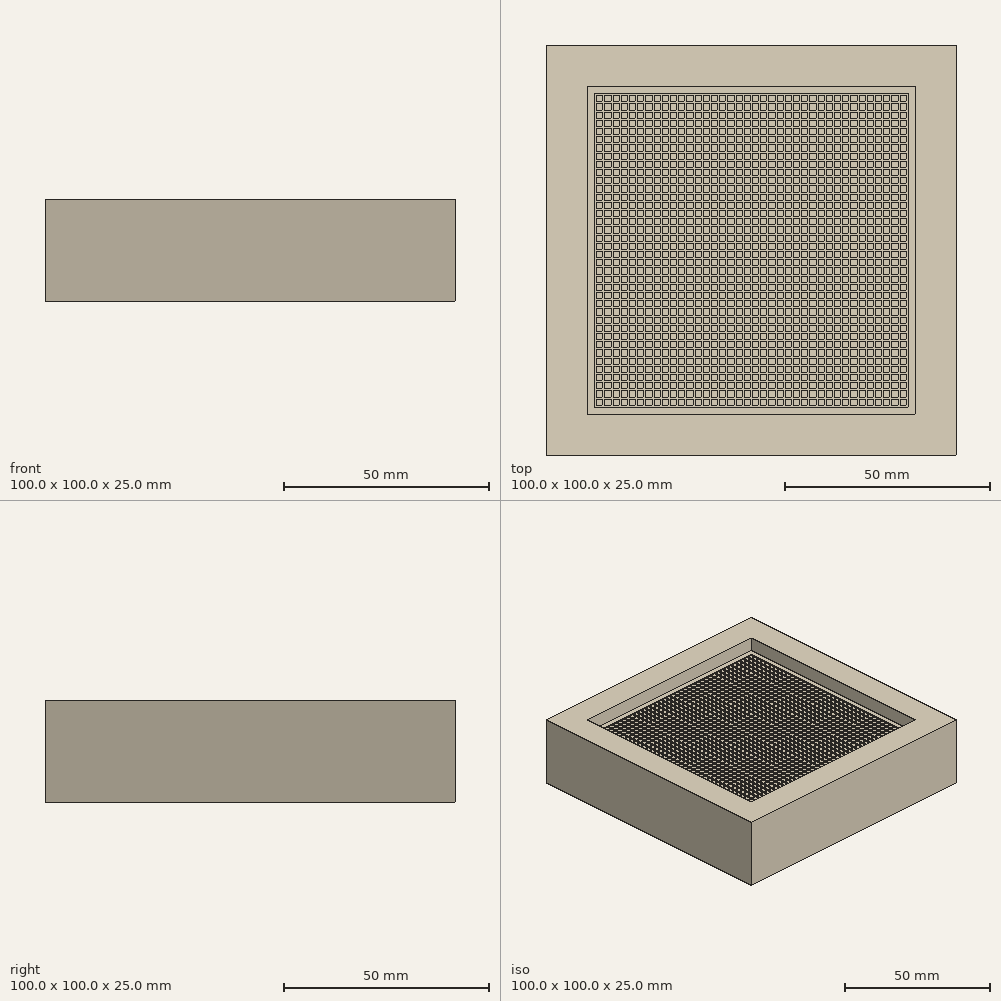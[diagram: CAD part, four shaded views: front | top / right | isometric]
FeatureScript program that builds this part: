
annotation { "Feature Type Name" : "Feature", "Feature Type Description" : "" }
export const myFeature = defineFeature(function(context is Context, id is Id, definition is map)
    precondition{}
    {
        {
            var Q0;
            Q0=qCreatedBy(makeId("Top.planeOp"),FACE);
            var sketch = newSketch(context, id + "F0", { "sketchPlane" : qUnion([Q0])});
            skLineSegment(sketch, "E0.bottom", {"start": v(0, 0) * mm, "end": v(100, 0) * mm});
            skLineSegment(sketch, "E0.top", {"start": v(0, 100) * mm, "end": v(100, 100) * mm});
            skLineSegment(sketch, "E0.left", {"start": v(0, 0) * mm, "end": v(0, 100) * mm});
            skLineSegment(sketch, "E0.right", {"start": v(100, 0) * mm, "end": v(100, 100) * mm});
            skSolve(sketch);
        }
        {
            var Q0;
            Q0 = qSketchRegion(id + "F0", true);
            extrude(context, id + "F1", {"entities" : qUnion([Q0]), "depth" : 25 * mm});
        }
        {
            var Q0;
            Q0=makeQuery(id+"F1.opExtrude","CAP_FACE",FACE,{"disambiguationData":[OSD([sQuery(id+"F0.wireOp",EDGE,"E0.bottom"),sQuery(id+"F0.wireOp",EDGE,"E0.top"),sQuery(id+"F0.wireOp",EDGE,"E0.left"),sQuery(id+"F0.wireOp",EDGE,"E0.right")])],"isStart":false});
            var sketch = newSketch(context, id + "F2", { "sketchPlane" : qUnion([Q0])});
            skLineSegment(sketch, "E1.bottom", {"start": v(10, 90) * mm, "end": v(90, 90) * mm});
            skLineSegment(sketch, "E1.top", {"start": v(10, 10) * mm, "end": v(90, 10) * mm});
            skLineSegment(sketch, "E1.left", {"start": v(10, 90) * mm, "end": v(10, 10) * mm});
            skLineSegment(sketch, "E1.right", {"start": v(90, 90) * mm, "end": v(90, 10) * mm});
            skSolve(sketch);
        }
        {
            var Q0;
            Q0 = qSketchRegion(id + "F2", true);
            extrude(context, id + "F3", {"entities" : qUnion([Q0]), "operationType" : NewBodyOperationType.REMOVE, "oppositeDirection" : true, "depth" : 5 * mm});
        }
        {
            var Q0;
            Q0=makeQuery(id+"F3.boolean.opBoolean","COPY",FACE,{"derivedFrom":makeQuery(id+"F3.opExtrude","CAP_FACE",FACE,{"disambiguationData":[OSD([sQuery(id+"F2.wireOp",EDGE,"E1.bottom"),sQuery(id+"F2.wireOp",EDGE,"E1.top"),sQuery(id+"F2.wireOp",EDGE,"E1.left"),sQuery(id+"F2.wireOp",EDGE,"E1.right")])],"isStart":false})});
            var sketch = newSketch(context, id + "F4", { "sketchPlane" : qUnion([Q0])});
            skLineSegment(sketch, "E2.bottom", {"start": v(11.75, 88.25) * mm, "end": v(12.25, 88.25) * mm});
            skLineSegment(sketch, "E2.top", {"start": v(11.75, 11.75) * mm, "end": v(12.25, 11.75) * mm});
            skLineSegment(sketch, "E2.left", {"start": v(11.75, 88.25) * mm, "end": v(11.75, 11.75) * mm});
            skLineSegment(sketch, "E2.right", {"start": v(12.25, 88.25) * mm, "end": v(12.25, 11.75) * mm});
            skLineSegment(sketch, "E3.1.0.0", {"start": v(13.75, 88.25) * mm, "end": v(14.25, 88.25) * mm});
            skLineSegment(sketch, "E3.1.0.1", {"start": v(13.75, 88.25) * mm, "end": v(13.75, 11.75) * mm});
            skLineSegment(sketch, "E3.1.0.2", {"start": v(14.25, 88.25) * mm, "end": v(14.25, 11.75) * mm});
            skLineSegment(sketch, "E3.1.0.3", {"start": v(13.75, 11.75) * mm, "end": v(14.25, 11.75) * mm});
            skLineSegment(sketch, "E3.2.0.0", {"start": v(15.75, 88.25) * mm, "end": v(16.25, 88.25) * mm});
            skLineSegment(sketch, "E3.2.0.1", {"start": v(15.75, 88.25) * mm, "end": v(15.75, 11.75) * mm});
            skLineSegment(sketch, "E3.2.0.2", {"start": v(16.25, 88.25) * mm, "end": v(16.25, 11.75) * mm});
            skLineSegment(sketch, "E3.2.0.3", {"start": v(15.75, 11.75) * mm, "end": v(16.25, 11.75) * mm});
            skLineSegment(sketch, "E3.3.0.0", {"start": v(17.75, 88.25) * mm, "end": v(18.25, 88.25) * mm});
            skLineSegment(sketch, "E3.3.0.1", {"start": v(17.75, 88.25) * mm, "end": v(17.75, 11.75) * mm});
            skLineSegment(sketch, "E3.3.0.2", {"start": v(18.25, 88.25) * mm, "end": v(18.25, 11.75) * mm});
            skLineSegment(sketch, "E3.3.0.3", {"start": v(17.75, 11.75) * mm, "end": v(18.25, 11.75) * mm});
            skLineSegment(sketch, "E3.4.0.0", {"start": v(19.75, 88.25) * mm, "end": v(20.25, 88.25) * mm});
            skLineSegment(sketch, "E3.4.0.1", {"start": v(19.75, 88.25) * mm, "end": v(19.75, 11.75) * mm});
            skLineSegment(sketch, "E3.4.0.2", {"start": v(20.25, 88.25) * mm, "end": v(20.25, 11.75) * mm});
            skLineSegment(sketch, "E3.4.0.3", {"start": v(19.75, 11.75) * mm, "end": v(20.25, 11.75) * mm});
            skLineSegment(sketch, "E3.5.0.0", {"start": v(21.75, 88.25) * mm, "end": v(22.25, 88.25) * mm});
            skLineSegment(sketch, "E3.5.0.1", {"start": v(21.75, 88.25) * mm, "end": v(21.75, 11.75) * mm});
            skLineSegment(sketch, "E3.5.0.2", {"start": v(22.25, 88.25) * mm, "end": v(22.25, 11.75) * mm});
            skLineSegment(sketch, "E3.5.0.3", {"start": v(21.75, 11.75) * mm, "end": v(22.25, 11.75) * mm});
            skLineSegment(sketch, "E3.6.0.0", {"start": v(23.75, 88.25) * mm, "end": v(24.25, 88.25) * mm});
            skLineSegment(sketch, "E3.6.0.1", {"start": v(23.75, 88.25) * mm, "end": v(23.75, 11.75) * mm});
            skLineSegment(sketch, "E3.6.0.2", {"start": v(24.25, 88.25) * mm, "end": v(24.25, 11.75) * mm});
            skLineSegment(sketch, "E3.6.0.3", {"start": v(23.75, 11.75) * mm, "end": v(24.25, 11.75) * mm});
            skLineSegment(sketch, "E3.7.0.0", {"start": v(25.75, 88.25) * mm, "end": v(26.25, 88.25) * mm});
            skLineSegment(sketch, "E3.7.0.1", {"start": v(25.75, 88.25) * mm, "end": v(25.75, 11.75) * mm});
            skLineSegment(sketch, "E3.7.0.2", {"start": v(26.25, 88.25) * mm, "end": v(26.25, 11.75) * mm});
            skLineSegment(sketch, "E3.7.0.3", {"start": v(25.75, 11.75) * mm, "end": v(26.25, 11.75) * mm});
            skLineSegment(sketch, "E3.8.0.0", {"start": v(27.75, 88.25) * mm, "end": v(28.25, 88.25) * mm});
            skLineSegment(sketch, "E3.8.0.1", {"start": v(27.75, 88.25) * mm, "end": v(27.75, 11.75) * mm});
            skLineSegment(sketch, "E3.8.0.2", {"start": v(28.25, 88.25) * mm, "end": v(28.25, 11.75) * mm});
            skLineSegment(sketch, "E3.8.0.3", {"start": v(27.75, 11.75) * mm, "end": v(28.25, 11.75) * mm});
            skLineSegment(sketch, "E3.9.0.0", {"start": v(29.75, 88.25) * mm, "end": v(30.25, 88.25) * mm});
            skLineSegment(sketch, "E3.9.0.1", {"start": v(29.75, 88.25) * mm, "end": v(29.75, 11.75) * mm});
            skLineSegment(sketch, "E3.9.0.2", {"start": v(30.25, 88.25) * mm, "end": v(30.25, 11.75) * mm});
            skLineSegment(sketch, "E3.9.0.3", {"start": v(29.75, 11.75) * mm, "end": v(30.25, 11.75) * mm});
            skLineSegment(sketch, "E3.10.0.0", {"start": v(31.75, 88.25) * mm, "end": v(32.25, 88.25) * mm});
            skLineSegment(sketch, "E3.10.0.1", {"start": v(31.75, 88.25) * mm, "end": v(31.75, 11.75) * mm});
            skLineSegment(sketch, "E3.10.0.2", {"start": v(32.25, 88.25) * mm, "end": v(32.25, 11.75) * mm});
            skLineSegment(sketch, "E3.10.0.3", {"start": v(31.75, 11.75) * mm, "end": v(32.25, 11.75) * mm});
            skLineSegment(sketch, "E3.11.0.0", {"start": v(33.75, 88.25) * mm, "end": v(34.25, 88.25) * mm});
            skLineSegment(sketch, "E3.11.0.1", {"start": v(33.75, 88.25) * mm, "end": v(33.75, 11.75) * mm});
            skLineSegment(sketch, "E3.11.0.2", {"start": v(34.25, 88.25) * mm, "end": v(34.25, 11.75) * mm});
            skLineSegment(sketch, "E3.11.0.3", {"start": v(33.75, 11.75) * mm, "end": v(34.25, 11.75) * mm});
            skLineSegment(sketch, "E3.12.0.0", {"start": v(35.75, 88.25) * mm, "end": v(36.25, 88.25) * mm});
            skLineSegment(sketch, "E3.12.0.1", {"start": v(35.75, 88.25) * mm, "end": v(35.75, 11.75) * mm});
            skLineSegment(sketch, "E3.12.0.2", {"start": v(36.25, 88.25) * mm, "end": v(36.25, 11.75) * mm});
            skLineSegment(sketch, "E3.12.0.3", {"start": v(35.75, 11.75) * mm, "end": v(36.25, 11.75) * mm});
            skLineSegment(sketch, "E3.13.0.0", {"start": v(37.75, 88.25) * mm, "end": v(38.25, 88.25) * mm});
            skLineSegment(sketch, "E3.13.0.1", {"start": v(37.75, 88.25) * mm, "end": v(37.75, 11.75) * mm});
            skLineSegment(sketch, "E3.13.0.2", {"start": v(38.25, 88.25) * mm, "end": v(38.25, 11.75) * mm});
            skLineSegment(sketch, "E3.13.0.3", {"start": v(37.75, 11.75) * mm, "end": v(38.25, 11.75) * mm});
            skLineSegment(sketch, "E3.14.0.0", {"start": v(39.75, 88.25) * mm, "end": v(40.25, 88.25) * mm});
            skLineSegment(sketch, "E3.14.0.1", {"start": v(39.75, 88.25) * mm, "end": v(39.75, 11.75) * mm});
            skLineSegment(sketch, "E3.14.0.2", {"start": v(40.25, 88.25) * mm, "end": v(40.25, 11.75) * mm});
            skLineSegment(sketch, "E3.14.0.3", {"start": v(39.75, 11.75) * mm, "end": v(40.25, 11.75) * mm});
            skLineSegment(sketch, "E3.15.0.0", {"start": v(41.75, 88.25) * mm, "end": v(42.25, 88.25) * mm});
            skLineSegment(sketch, "E3.15.0.1", {"start": v(41.75, 88.25) * mm, "end": v(41.75, 11.75) * mm});
            skLineSegment(sketch, "E3.15.0.2", {"start": v(42.25, 88.25) * mm, "end": v(42.25, 11.75) * mm});
            skLineSegment(sketch, "E3.15.0.3", {"start": v(41.75, 11.75) * mm, "end": v(42.25, 11.75) * mm});
            skLineSegment(sketch, "E3.16.0.0", {"start": v(43.75, 88.25) * mm, "end": v(44.25, 88.25) * mm});
            skLineSegment(sketch, "E3.16.0.1", {"start": v(43.75, 88.25) * mm, "end": v(43.75, 11.75) * mm});
            skLineSegment(sketch, "E3.16.0.2", {"start": v(44.25, 88.25) * mm, "end": v(44.25, 11.75) * mm});
            skLineSegment(sketch, "E3.16.0.3", {"start": v(43.75, 11.75) * mm, "end": v(44.25, 11.75) * mm});
            skLineSegment(sketch, "E3.17.0.0", {"start": v(45.75, 88.25) * mm, "end": v(46.25, 88.25) * mm});
            skLineSegment(sketch, "E3.17.0.1", {"start": v(45.75, 88.25) * mm, "end": v(45.75, 11.75) * mm});
            skLineSegment(sketch, "E3.17.0.2", {"start": v(46.25, 88.25) * mm, "end": v(46.25, 11.75) * mm});
            skLineSegment(sketch, "E3.17.0.3", {"start": v(45.75, 11.75) * mm, "end": v(46.25, 11.75) * mm});
            skLineSegment(sketch, "E3.18.0.0", {"start": v(47.75, 88.25) * mm, "end": v(48.25, 88.25) * mm});
            skLineSegment(sketch, "E3.18.0.1", {"start": v(47.75, 88.25) * mm, "end": v(47.75, 11.75) * mm});
            skLineSegment(sketch, "E3.18.0.2", {"start": v(48.25, 88.25) * mm, "end": v(48.25, 11.75) * mm});
            skLineSegment(sketch, "E3.18.0.3", {"start": v(47.75, 11.75) * mm, "end": v(48.25, 11.75) * mm});
            skLineSegment(sketch, "E3.19.0.0", {"start": v(49.75, 88.25) * mm, "end": v(50.25, 88.25) * mm});
            skLineSegment(sketch, "E3.19.0.1", {"start": v(49.75, 88.25) * mm, "end": v(49.75, 11.75) * mm});
            skLineSegment(sketch, "E3.19.0.2", {"start": v(50.25, 88.25) * mm, "end": v(50.25, 11.75) * mm});
            skLineSegment(sketch, "E3.19.0.3", {"start": v(49.75, 11.75) * mm, "end": v(50.25, 11.75) * mm});
            skLineSegment(sketch, "E3.20.0.0", {"start": v(51.75, 88.25) * mm, "end": v(52.25, 88.25) * mm});
            skLineSegment(sketch, "E3.20.0.1", {"start": v(51.75, 88.25) * mm, "end": v(51.75, 11.75) * mm});
            skLineSegment(sketch, "E3.20.0.2", {"start": v(52.25, 88.25) * mm, "end": v(52.25, 11.75) * mm});
            skLineSegment(sketch, "E3.20.0.3", {"start": v(51.75, 11.75) * mm, "end": v(52.25, 11.75) * mm});
            skLineSegment(sketch, "E3.21.0.0", {"start": v(53.75, 88.25) * mm, "end": v(54.25, 88.25) * mm});
            skLineSegment(sketch, "E3.21.0.1", {"start": v(53.75, 88.25) * mm, "end": v(53.75, 11.75) * mm});
            skLineSegment(sketch, "E3.21.0.2", {"start": v(54.25, 88.25) * mm, "end": v(54.25, 11.75) * mm});
            skLineSegment(sketch, "E3.21.0.3", {"start": v(53.75, 11.75) * mm, "end": v(54.25, 11.75) * mm});
            skLineSegment(sketch, "E3.22.0.0", {"start": v(55.75, 88.25) * mm, "end": v(56.25, 88.25) * mm});
            skLineSegment(sketch, "E3.22.0.1", {"start": v(55.75, 88.25) * mm, "end": v(55.75, 11.75) * mm});
            skLineSegment(sketch, "E3.22.0.2", {"start": v(56.25, 88.25) * mm, "end": v(56.25, 11.75) * mm});
            skLineSegment(sketch, "E3.22.0.3", {"start": v(55.75, 11.75) * mm, "end": v(56.25, 11.75) * mm});
            skLineSegment(sketch, "E3.23.0.0", {"start": v(57.75, 88.25) * mm, "end": v(58.25, 88.25) * mm});
            skLineSegment(sketch, "E3.23.0.1", {"start": v(57.75, 88.25) * mm, "end": v(57.75, 11.75) * mm});
            skLineSegment(sketch, "E3.23.0.2", {"start": v(58.25, 88.25) * mm, "end": v(58.25, 11.75) * mm});
            skLineSegment(sketch, "E3.23.0.3", {"start": v(57.75, 11.75) * mm, "end": v(58.25, 11.75) * mm});
            skLineSegment(sketch, "E3.24.0.0", {"start": v(59.75, 88.25) * mm, "end": v(60.25, 88.25) * mm});
            skLineSegment(sketch, "E3.24.0.1", {"start": v(59.75, 88.25) * mm, "end": v(59.75, 11.75) * mm});
            skLineSegment(sketch, "E3.24.0.2", {"start": v(60.25, 88.25) * mm, "end": v(60.25, 11.75) * mm});
            skLineSegment(sketch, "E3.24.0.3", {"start": v(59.75, 11.75) * mm, "end": v(60.25, 11.75) * mm});
            skLineSegment(sketch, "E3.25.0.0", {"start": v(61.75, 88.25) * mm, "end": v(62.25, 88.25) * mm});
            skLineSegment(sketch, "E3.25.0.1", {"start": v(61.75, 88.25) * mm, "end": v(61.75, 11.75) * mm});
            skLineSegment(sketch, "E3.25.0.2", {"start": v(62.25, 88.25) * mm, "end": v(62.25, 11.75) * mm});
            skLineSegment(sketch, "E3.25.0.3", {"start": v(61.75, 11.75) * mm, "end": v(62.25, 11.75) * mm});
            skLineSegment(sketch, "E3.26.0.0", {"start": v(63.75, 88.25) * mm, "end": v(64.25, 88.25) * mm});
            skLineSegment(sketch, "E3.26.0.1", {"start": v(63.75, 88.25) * mm, "end": v(63.75, 11.75) * mm});
            skLineSegment(sketch, "E3.26.0.2", {"start": v(64.25, 88.25) * mm, "end": v(64.25, 11.75) * mm});
            skLineSegment(sketch, "E3.26.0.3", {"start": v(63.75, 11.75) * mm, "end": v(64.25, 11.75) * mm});
            skLineSegment(sketch, "E3.27.0.0", {"start": v(65.75, 88.25) * mm, "end": v(66.25, 88.25) * mm});
            skLineSegment(sketch, "E3.27.0.1", {"start": v(65.75, 88.25) * mm, "end": v(65.75, 11.75) * mm});
            skLineSegment(sketch, "E3.27.0.2", {"start": v(66.25, 88.25) * mm, "end": v(66.25, 11.75) * mm});
            skLineSegment(sketch, "E3.27.0.3", {"start": v(65.75, 11.75) * mm, "end": v(66.25, 11.75) * mm});
            skLineSegment(sketch, "E3.28.0.0", {"start": v(67.75, 88.25) * mm, "end": v(68.25, 88.25) * mm});
            skLineSegment(sketch, "E3.28.0.1", {"start": v(67.75, 88.25) * mm, "end": v(67.75, 11.75) * mm});
            skLineSegment(sketch, "E3.28.0.2", {"start": v(68.25, 88.25) * mm, "end": v(68.25, 11.75) * mm});
            skLineSegment(sketch, "E3.28.0.3", {"start": v(67.75, 11.75) * mm, "end": v(68.25, 11.75) * mm});
            skLineSegment(sketch, "E3.29.0.0", {"start": v(69.75, 88.25) * mm, "end": v(70.25, 88.25) * mm});
            skLineSegment(sketch, "E3.29.0.1", {"start": v(69.75, 88.25) * mm, "end": v(69.75, 11.75) * mm});
            skLineSegment(sketch, "E3.29.0.2", {"start": v(70.25, 88.25) * mm, "end": v(70.25, 11.75) * mm});
            skLineSegment(sketch, "E3.29.0.3", {"start": v(69.75, 11.75) * mm, "end": v(70.25, 11.75) * mm});
            skLineSegment(sketch, "E3.30.0.0", {"start": v(71.75, 88.25) * mm, "end": v(72.25, 88.25) * mm});
            skLineSegment(sketch, "E3.30.0.1", {"start": v(71.75, 88.25) * mm, "end": v(71.75, 11.75) * mm});
            skLineSegment(sketch, "E3.30.0.2", {"start": v(72.25, 88.25) * mm, "end": v(72.25, 11.75) * mm});
            skLineSegment(sketch, "E3.30.0.3", {"start": v(71.75, 11.75) * mm, "end": v(72.25, 11.75) * mm});
            skLineSegment(sketch, "E3.31.0.0", {"start": v(73.75, 88.25) * mm, "end": v(74.25, 88.25) * mm});
            skLineSegment(sketch, "E3.31.0.1", {"start": v(73.75, 88.25) * mm, "end": v(73.75, 11.75) * mm});
            skLineSegment(sketch, "E3.31.0.2", {"start": v(74.25, 88.25) * mm, "end": v(74.25, 11.75) * mm});
            skLineSegment(sketch, "E3.31.0.3", {"start": v(73.75, 11.75) * mm, "end": v(74.25, 11.75) * mm});
            skLineSegment(sketch, "E3.32.0.0", {"start": v(75.75, 88.25) * mm, "end": v(76.25, 88.25) * mm});
            skLineSegment(sketch, "E3.32.0.1", {"start": v(75.75, 88.25) * mm, "end": v(75.75, 11.75) * mm});
            skLineSegment(sketch, "E3.32.0.2", {"start": v(76.25, 88.25) * mm, "end": v(76.25, 11.75) * mm});
            skLineSegment(sketch, "E3.32.0.3", {"start": v(75.75, 11.75) * mm, "end": v(76.25, 11.75) * mm});
            skLineSegment(sketch, "E3.33.0.0", {"start": v(77.75, 88.25) * mm, "end": v(78.25, 88.25) * mm});
            skLineSegment(sketch, "E3.33.0.1", {"start": v(77.75, 88.25) * mm, "end": v(77.75, 11.75) * mm});
            skLineSegment(sketch, "E3.33.0.2", {"start": v(78.25, 88.25) * mm, "end": v(78.25, 11.75) * mm});
            skLineSegment(sketch, "E3.33.0.3", {"start": v(77.75, 11.75) * mm, "end": v(78.25, 11.75) * mm});
            skLineSegment(sketch, "E3.34.0.0", {"start": v(79.75, 88.25) * mm, "end": v(80.25, 88.25) * mm});
            skLineSegment(sketch, "E3.34.0.1", {"start": v(79.75, 88.25) * mm, "end": v(79.75, 11.75) * mm});
            skLineSegment(sketch, "E3.34.0.2", {"start": v(80.25, 88.25) * mm, "end": v(80.25, 11.75) * mm});
            skLineSegment(sketch, "E3.34.0.3", {"start": v(79.75, 11.75) * mm, "end": v(80.25, 11.75) * mm});
            skLineSegment(sketch, "E3.35.0.0", {"start": v(81.75, 88.25) * mm, "end": v(82.25, 88.25) * mm});
            skLineSegment(sketch, "E3.35.0.1", {"start": v(81.75, 88.25) * mm, "end": v(81.75, 11.75) * mm});
            skLineSegment(sketch, "E3.35.0.2", {"start": v(82.25, 88.25) * mm, "end": v(82.25, 11.75) * mm});
            skLineSegment(sketch, "E3.35.0.3", {"start": v(81.75, 11.75) * mm, "end": v(82.25, 11.75) * mm});
            skLineSegment(sketch, "E3.36.0.0", {"start": v(83.75, 88.25) * mm, "end": v(84.25, 88.25) * mm});
            skLineSegment(sketch, "E3.36.0.1", {"start": v(83.75, 88.25) * mm, "end": v(83.75, 11.75) * mm});
            skLineSegment(sketch, "E3.36.0.2", {"start": v(84.25, 88.25) * mm, "end": v(84.25, 11.75) * mm});
            skLineSegment(sketch, "E3.36.0.3", {"start": v(83.75, 11.75) * mm, "end": v(84.25, 11.75) * mm});
            skLineSegment(sketch, "E3.37.0.0", {"start": v(85.75, 88.25) * mm, "end": v(86.25, 88.25) * mm});
            skLineSegment(sketch, "E3.37.0.1", {"start": v(85.75, 88.25) * mm, "end": v(85.75, 11.75) * mm});
            skLineSegment(sketch, "E3.37.0.2", {"start": v(86.25, 88.25) * mm, "end": v(86.25, 11.75) * mm});
            skLineSegment(sketch, "E3.37.0.3", {"start": v(85.75, 11.75) * mm, "end": v(86.25, 11.75) * mm});
            skLineSegment(sketch, "E3.38.0.0", {"start": v(87.75, 88.25) * mm, "end": v(88.25, 88.25) * mm});
            skLineSegment(sketch, "E3.38.0.1", {"start": v(87.75, 88.25) * mm, "end": v(87.75, 11.75) * mm});
            skLineSegment(sketch, "E3.38.0.2", {"start": v(88.25, 88.25) * mm, "end": v(88.25, 11.75) * mm});
            skLineSegment(sketch, "E3.38.0.3", {"start": v(87.75, 11.75) * mm, "end": v(88.25, 11.75) * mm});
            skLineSegment(sketch, "E3.direction1", {"start": v(11.75, 88.25) * mm, "end": v(13.75, 88.25) * mm, "construction": true});
            skSolve(sketch);
        }
        {
            var Q0;
            Q0 = qSketchRegion(id + "F4", true);
            extrude(context, id + "F5", {"entities" : qUnion([Q0]), "operationType" : NewBodyOperationType.REMOVE, "oppositeDirection" : true, "depth" : 0.2 * mm});
        }
        {
            var Q0;
            Q0=makeQuery(id+"F3.boolean.opBoolean","COPY",FACE,{"derivedFrom":makeQuery(id+"F3.opExtrude","CAP_FACE",FACE,{"disambiguationData":[OSD([sQuery(id+"F2.wireOp",EDGE,"E1.bottom"),sQuery(id+"F2.wireOp",EDGE,"E1.top"),sQuery(id+"F2.wireOp",EDGE,"E1.left"),sQuery(id+"F2.wireOp",EDGE,"E1.right")])],"isStart":false})});
            var sketch = newSketch(context, id + "F6", { "sketchPlane" : qUnion([Q0])});
            skLineSegment(sketch, "E4.bottom", {"start": v(12, 88.25) * mm, "end": v(88, 88.25) * mm});
            skLineSegment(sketch, "E4.top", {"start": v(12, 87.75) * mm, "end": v(88, 87.75) * mm});
            skLineSegment(sketch, "E4.left", {"start": v(12, 88.25) * mm, "end": v(12, 87.75) * mm});
            skLineSegment(sketch, "E4.right", {"start": v(88, 88.25) * mm, "end": v(88, 87.75) * mm});
            skLineSegment(sketch, "E5.0.1.0", {"start": v(12, 85.75) * mm, "end": v(88, 85.75) * mm});
            skLineSegment(sketch, "E5.0.1.1", {"start": v(12, 86.25) * mm, "end": v(88, 86.25) * mm});
            skLineSegment(sketch, "E5.0.1.2", {"start": v(12, 86.25) * mm, "end": v(12, 85.75) * mm});
            skLineSegment(sketch, "E5.0.1.3", {"start": v(88, 86.25) * mm, "end": v(88, 85.75) * mm});
            skLineSegment(sketch, "E5.0.2.0", {"start": v(12, 83.75) * mm, "end": v(88, 83.75) * mm});
            skLineSegment(sketch, "E5.0.2.1", {"start": v(12, 84.25) * mm, "end": v(88, 84.25) * mm});
            skLineSegment(sketch, "E5.0.2.2", {"start": v(12, 84.25) * mm, "end": v(12, 83.75) * mm});
            skLineSegment(sketch, "E5.0.2.3", {"start": v(88, 84.25) * mm, "end": v(88, 83.75) * mm});
            skLineSegment(sketch, "E5.0.3.0", {"start": v(12, 81.75) * mm, "end": v(88, 81.75) * mm});
            skLineSegment(sketch, "E5.0.3.1", {"start": v(12, 82.25) * mm, "end": v(88, 82.25) * mm});
            skLineSegment(sketch, "E5.0.3.2", {"start": v(12, 82.25) * mm, "end": v(12, 81.75) * mm});
            skLineSegment(sketch, "E5.0.3.3", {"start": v(88, 82.25) * mm, "end": v(88, 81.75) * mm});
            skLineSegment(sketch, "E5.0.4.0", {"start": v(12, 79.75) * mm, "end": v(88, 79.75) * mm});
            skLineSegment(sketch, "E5.0.4.1", {"start": v(12, 80.25) * mm, "end": v(88, 80.25) * mm});
            skLineSegment(sketch, "E5.0.4.2", {"start": v(12, 80.25) * mm, "end": v(12, 79.75) * mm});
            skLineSegment(sketch, "E5.0.4.3", {"start": v(88, 80.25) * mm, "end": v(88, 79.75) * mm});
            skLineSegment(sketch, "E5.0.5.0", {"start": v(12, 77.75) * mm, "end": v(88, 77.75) * mm});
            skLineSegment(sketch, "E5.0.5.1", {"start": v(12, 78.25) * mm, "end": v(88, 78.25) * mm});
            skLineSegment(sketch, "E5.0.5.2", {"start": v(12, 78.25) * mm, "end": v(12, 77.75) * mm});
            skLineSegment(sketch, "E5.0.5.3", {"start": v(88, 78.25) * mm, "end": v(88, 77.75) * mm});
            skLineSegment(sketch, "E5.0.6.0", {"start": v(12, 75.75) * mm, "end": v(88, 75.75) * mm});
            skLineSegment(sketch, "E5.0.6.1", {"start": v(12, 76.25) * mm, "end": v(88, 76.25) * mm});
            skLineSegment(sketch, "E5.0.6.2", {"start": v(12, 76.25) * mm, "end": v(12, 75.75) * mm});
            skLineSegment(sketch, "E5.0.6.3", {"start": v(88, 76.25) * mm, "end": v(88, 75.75) * mm});
            skLineSegment(sketch, "E5.0.7.0", {"start": v(12, 73.75) * mm, "end": v(88, 73.75) * mm});
            skLineSegment(sketch, "E5.0.7.1", {"start": v(12, 74.25) * mm, "end": v(88, 74.25) * mm});
            skLineSegment(sketch, "E5.0.7.2", {"start": v(12, 74.25) * mm, "end": v(12, 73.75) * mm});
            skLineSegment(sketch, "E5.0.7.3", {"start": v(88, 74.25) * mm, "end": v(88, 73.75) * mm});
            skLineSegment(sketch, "E5.0.8.0", {"start": v(12, 71.75) * mm, "end": v(88, 71.75) * mm});
            skLineSegment(sketch, "E5.0.8.1", {"start": v(12, 72.25) * mm, "end": v(88, 72.25) * mm});
            skLineSegment(sketch, "E5.0.8.2", {"start": v(12, 72.25) * mm, "end": v(12, 71.75) * mm});
            skLineSegment(sketch, "E5.0.8.3", {"start": v(88, 72.25) * mm, "end": v(88, 71.75) * mm});
            skLineSegment(sketch, "E5.0.9.0", {"start": v(12, 69.75) * mm, "end": v(88, 69.75) * mm});
            skLineSegment(sketch, "E5.0.9.1", {"start": v(12, 70.25) * mm, "end": v(88, 70.25) * mm});
            skLineSegment(sketch, "E5.0.9.2", {"start": v(12, 70.25) * mm, "end": v(12, 69.75) * mm});
            skLineSegment(sketch, "E5.0.9.3", {"start": v(88, 70.25) * mm, "end": v(88, 69.75) * mm});
            skLineSegment(sketch, "E5.0.10.0", {"start": v(12, 67.75) * mm, "end": v(88, 67.75) * mm});
            skLineSegment(sketch, "E5.0.10.1", {"start": v(12, 68.25) * mm, "end": v(88, 68.25) * mm});
            skLineSegment(sketch, "E5.0.10.2", {"start": v(12, 68.25) * mm, "end": v(12, 67.75) * mm});
            skLineSegment(sketch, "E5.0.10.3", {"start": v(88, 68.25) * mm, "end": v(88, 67.75) * mm});
            skLineSegment(sketch, "E5.0.11.0", {"start": v(12, 65.75) * mm, "end": v(88, 65.75) * mm});
            skLineSegment(sketch, "E5.0.11.1", {"start": v(12, 66.25) * mm, "end": v(88, 66.25) * mm});
            skLineSegment(sketch, "E5.0.11.2", {"start": v(12, 66.25) * mm, "end": v(12, 65.75) * mm});
            skLineSegment(sketch, "E5.0.11.3", {"start": v(88, 66.25) * mm, "end": v(88, 65.75) * mm});
            skLineSegment(sketch, "E5.0.12.0", {"start": v(12, 63.75) * mm, "end": v(88, 63.75) * mm});
            skLineSegment(sketch, "E5.0.12.1", {"start": v(12, 64.25) * mm, "end": v(88, 64.25) * mm});
            skLineSegment(sketch, "E5.0.12.2", {"start": v(12, 64.25) * mm, "end": v(12, 63.75) * mm});
            skLineSegment(sketch, "E5.0.12.3", {"start": v(88, 64.25) * mm, "end": v(88, 63.75) * mm});
            skLineSegment(sketch, "E5.0.13.0", {"start": v(12, 61.75) * mm, "end": v(88, 61.75) * mm});
            skLineSegment(sketch, "E5.0.13.1", {"start": v(12, 62.25) * mm, "end": v(88, 62.25) * mm});
            skLineSegment(sketch, "E5.0.13.2", {"start": v(12, 62.25) * mm, "end": v(12, 61.75) * mm});
            skLineSegment(sketch, "E5.0.13.3", {"start": v(88, 62.25) * mm, "end": v(88, 61.75) * mm});
            skLineSegment(sketch, "E5.0.14.0", {"start": v(12, 59.75) * mm, "end": v(88, 59.75) * mm});
            skLineSegment(sketch, "E5.0.14.1", {"start": v(12, 60.25) * mm, "end": v(88, 60.25) * mm});
            skLineSegment(sketch, "E5.0.14.2", {"start": v(12, 60.25) * mm, "end": v(12, 59.75) * mm});
            skLineSegment(sketch, "E5.0.14.3", {"start": v(88, 60.25) * mm, "end": v(88, 59.75) * mm});
            skLineSegment(sketch, "E5.0.15.0", {"start": v(12, 57.75) * mm, "end": v(88, 57.75) * mm});
            skLineSegment(sketch, "E5.0.15.1", {"start": v(12, 58.25) * mm, "end": v(88, 58.25) * mm});
            skLineSegment(sketch, "E5.0.15.2", {"start": v(12, 58.25) * mm, "end": v(12, 57.75) * mm});
            skLineSegment(sketch, "E5.0.15.3", {"start": v(88, 58.25) * mm, "end": v(88, 57.75) * mm});
            skLineSegment(sketch, "E5.0.16.0", {"start": v(12, 55.75) * mm, "end": v(88, 55.75) * mm});
            skLineSegment(sketch, "E5.0.16.1", {"start": v(12, 56.25) * mm, "end": v(88, 56.25) * mm});
            skLineSegment(sketch, "E5.0.16.2", {"start": v(12, 56.25) * mm, "end": v(12, 55.75) * mm});
            skLineSegment(sketch, "E5.0.16.3", {"start": v(88, 56.25) * mm, "end": v(88, 55.75) * mm});
            skLineSegment(sketch, "E5.0.17.0", {"start": v(12, 53.75) * mm, "end": v(88, 53.75) * mm});
            skLineSegment(sketch, "E5.0.17.1", {"start": v(12, 54.25) * mm, "end": v(88, 54.25) * mm});
            skLineSegment(sketch, "E5.0.17.2", {"start": v(12, 54.25) * mm, "end": v(12, 53.75) * mm});
            skLineSegment(sketch, "E5.0.17.3", {"start": v(88, 54.25) * mm, "end": v(88, 53.75) * mm});
            skLineSegment(sketch, "E5.0.18.0", {"start": v(12, 51.75) * mm, "end": v(88, 51.75) * mm});
            skLineSegment(sketch, "E5.0.18.1", {"start": v(12, 52.25) * mm, "end": v(88, 52.25) * mm});
            skLineSegment(sketch, "E5.0.18.2", {"start": v(12, 52.25) * mm, "end": v(12, 51.75) * mm});
            skLineSegment(sketch, "E5.0.18.3", {"start": v(88, 52.25) * mm, "end": v(88, 51.75) * mm});
            skLineSegment(sketch, "E5.0.19.0", {"start": v(12, 49.75) * mm, "end": v(88, 49.75) * mm});
            skLineSegment(sketch, "E5.0.19.1", {"start": v(12, 50.25) * mm, "end": v(88, 50.25) * mm});
            skLineSegment(sketch, "E5.0.19.2", {"start": v(12, 50.25) * mm, "end": v(12, 49.75) * mm});
            skLineSegment(sketch, "E5.0.19.3", {"start": v(88, 50.25) * mm, "end": v(88, 49.75) * mm});
            skLineSegment(sketch, "E5.0.20.0", {"start": v(12, 47.75) * mm, "end": v(88, 47.75) * mm});
            skLineSegment(sketch, "E5.0.20.1", {"start": v(12, 48.25) * mm, "end": v(88, 48.25) * mm});
            skLineSegment(sketch, "E5.0.20.2", {"start": v(12, 48.25) * mm, "end": v(12, 47.75) * mm});
            skLineSegment(sketch, "E5.0.20.3", {"start": v(88, 48.25) * mm, "end": v(88, 47.75) * mm});
            skLineSegment(sketch, "E5.0.21.0", {"start": v(12, 45.75) * mm, "end": v(88, 45.75) * mm});
            skLineSegment(sketch, "E5.0.21.1", {"start": v(12, 46.25) * mm, "end": v(88, 46.25) * mm});
            skLineSegment(sketch, "E5.0.21.2", {"start": v(12, 46.25) * mm, "end": v(12, 45.75) * mm});
            skLineSegment(sketch, "E5.0.21.3", {"start": v(88, 46.25) * mm, "end": v(88, 45.75) * mm});
            skLineSegment(sketch, "E5.0.22.0", {"start": v(12, 43.75) * mm, "end": v(88, 43.75) * mm});
            skLineSegment(sketch, "E5.0.22.1", {"start": v(12, 44.25) * mm, "end": v(88, 44.25) * mm});
            skLineSegment(sketch, "E5.0.22.2", {"start": v(12, 44.25) * mm, "end": v(12, 43.75) * mm});
            skLineSegment(sketch, "E5.0.22.3", {"start": v(88, 44.25) * mm, "end": v(88, 43.75) * mm});
            skLineSegment(sketch, "E5.0.23.0", {"start": v(12, 41.75) * mm, "end": v(88, 41.75) * mm});
            skLineSegment(sketch, "E5.0.23.1", {"start": v(12, 42.25) * mm, "end": v(88, 42.25) * mm});
            skLineSegment(sketch, "E5.0.23.2", {"start": v(12, 42.25) * mm, "end": v(12, 41.75) * mm});
            skLineSegment(sketch, "E5.0.23.3", {"start": v(88, 42.25) * mm, "end": v(88, 41.75) * mm});
            skLineSegment(sketch, "E5.0.24.0", {"start": v(12, 39.75) * mm, "end": v(88, 39.75) * mm});
            skLineSegment(sketch, "E5.0.24.1", {"start": v(12, 40.25) * mm, "end": v(88, 40.25) * mm});
            skLineSegment(sketch, "E5.0.24.2", {"start": v(12, 40.25) * mm, "end": v(12, 39.75) * mm});
            skLineSegment(sketch, "E5.0.24.3", {"start": v(88, 40.25) * mm, "end": v(88, 39.75) * mm});
            skLineSegment(sketch, "E5.0.25.0", {"start": v(12, 37.75) * mm, "end": v(88, 37.75) * mm});
            skLineSegment(sketch, "E5.0.25.1", {"start": v(12, 38.25) * mm, "end": v(88, 38.25) * mm});
            skLineSegment(sketch, "E5.0.25.2", {"start": v(12, 38.25) * mm, "end": v(12, 37.75) * mm});
            skLineSegment(sketch, "E5.0.25.3", {"start": v(88, 38.25) * mm, "end": v(88, 37.75) * mm});
            skLineSegment(sketch, "E5.0.26.0", {"start": v(12, 35.75) * mm, "end": v(88, 35.75) * mm});
            skLineSegment(sketch, "E5.0.26.1", {"start": v(12, 36.25) * mm, "end": v(88, 36.25) * mm});
            skLineSegment(sketch, "E5.0.26.2", {"start": v(12, 36.25) * mm, "end": v(12, 35.75) * mm});
            skLineSegment(sketch, "E5.0.26.3", {"start": v(88, 36.25) * mm, "end": v(88, 35.75) * mm});
            skLineSegment(sketch, "E5.0.27.0", {"start": v(12, 33.75) * mm, "end": v(88, 33.75) * mm});
            skLineSegment(sketch, "E5.0.27.1", {"start": v(12, 34.25) * mm, "end": v(88, 34.25) * mm});
            skLineSegment(sketch, "E5.0.27.2", {"start": v(12, 34.25) * mm, "end": v(12, 33.75) * mm});
            skLineSegment(sketch, "E5.0.27.3", {"start": v(88, 34.25) * mm, "end": v(88, 33.75) * mm});
            skLineSegment(sketch, "E5.0.28.0", {"start": v(12, 31.75) * mm, "end": v(88, 31.75) * mm});
            skLineSegment(sketch, "E5.0.28.1", {"start": v(12, 32.25) * mm, "end": v(88, 32.25) * mm});
            skLineSegment(sketch, "E5.0.28.2", {"start": v(12, 32.25) * mm, "end": v(12, 31.75) * mm});
            skLineSegment(sketch, "E5.0.28.3", {"start": v(88, 32.25) * mm, "end": v(88, 31.75) * mm});
            skLineSegment(sketch, "E5.0.29.0", {"start": v(12, 29.75) * mm, "end": v(88, 29.75) * mm});
            skLineSegment(sketch, "E5.0.29.1", {"start": v(12, 30.25) * mm, "end": v(88, 30.25) * mm});
            skLineSegment(sketch, "E5.0.29.2", {"start": v(12, 30.25) * mm, "end": v(12, 29.75) * mm});
            skLineSegment(sketch, "E5.0.29.3", {"start": v(88, 30.25) * mm, "end": v(88, 29.75) * mm});
            skLineSegment(sketch, "E5.0.30.0", {"start": v(12, 27.75) * mm, "end": v(88, 27.75) * mm});
            skLineSegment(sketch, "E5.0.30.1", {"start": v(12, 28.25) * mm, "end": v(88, 28.25) * mm});
            skLineSegment(sketch, "E5.0.30.2", {"start": v(12, 28.25) * mm, "end": v(12, 27.75) * mm});
            skLineSegment(sketch, "E5.0.30.3", {"start": v(88, 28.25) * mm, "end": v(88, 27.75) * mm});
            skLineSegment(sketch, "E5.0.31.0", {"start": v(12, 25.75) * mm, "end": v(88, 25.75) * mm});
            skLineSegment(sketch, "E5.0.31.1", {"start": v(12, 26.25) * mm, "end": v(88, 26.25) * mm});
            skLineSegment(sketch, "E5.0.31.2", {"start": v(12, 26.25) * mm, "end": v(12, 25.75) * mm});
            skLineSegment(sketch, "E5.0.31.3", {"start": v(88, 26.25) * mm, "end": v(88, 25.75) * mm});
            skLineSegment(sketch, "E5.0.32.0", {"start": v(12, 23.75) * mm, "end": v(88, 23.75) * mm});
            skLineSegment(sketch, "E5.0.32.1", {"start": v(12, 24.25) * mm, "end": v(88, 24.25) * mm});
            skLineSegment(sketch, "E5.0.32.2", {"start": v(12, 24.25) * mm, "end": v(12, 23.75) * mm});
            skLineSegment(sketch, "E5.0.32.3", {"start": v(88, 24.25) * mm, "end": v(88, 23.75) * mm});
            skLineSegment(sketch, "E5.0.33.0", {"start": v(12, 21.75) * mm, "end": v(88, 21.75) * mm});
            skLineSegment(sketch, "E5.0.33.1", {"start": v(12, 22.25) * mm, "end": v(88, 22.25) * mm});
            skLineSegment(sketch, "E5.0.33.2", {"start": v(12, 22.25) * mm, "end": v(12, 21.75) * mm});
            skLineSegment(sketch, "E5.0.33.3", {"start": v(88, 22.25) * mm, "end": v(88, 21.75) * mm});
            skLineSegment(sketch, "E5.0.34.0", {"start": v(12, 19.75) * mm, "end": v(88, 19.75) * mm});
            skLineSegment(sketch, "E5.0.34.1", {"start": v(12, 20.25) * mm, "end": v(88, 20.25) * mm});
            skLineSegment(sketch, "E5.0.34.2", {"start": v(12, 20.25) * mm, "end": v(12, 19.75) * mm});
            skLineSegment(sketch, "E5.0.34.3", {"start": v(88, 20.25) * mm, "end": v(88, 19.75) * mm});
            skLineSegment(sketch, "E5.0.35.0", {"start": v(12, 17.75) * mm, "end": v(88, 17.75) * mm});
            skLineSegment(sketch, "E5.0.35.1", {"start": v(12, 18.25) * mm, "end": v(88, 18.25) * mm});
            skLineSegment(sketch, "E5.0.35.2", {"start": v(12, 18.25) * mm, "end": v(12, 17.75) * mm});
            skLineSegment(sketch, "E5.0.35.3", {"start": v(88, 18.25) * mm, "end": v(88, 17.75) * mm});
            skLineSegment(sketch, "E5.0.36.0", {"start": v(12, 15.75) * mm, "end": v(88, 15.75) * mm});
            skLineSegment(sketch, "E5.0.36.1", {"start": v(12, 16.25) * mm, "end": v(88, 16.25) * mm});
            skLineSegment(sketch, "E5.0.36.2", {"start": v(12, 16.25) * mm, "end": v(12, 15.75) * mm});
            skLineSegment(sketch, "E5.0.36.3", {"start": v(88, 16.25) * mm, "end": v(88, 15.75) * mm});
            skLineSegment(sketch, "E5.0.37.0", {"start": v(12, 13.75) * mm, "end": v(88, 13.75) * mm});
            skLineSegment(sketch, "E5.0.37.1", {"start": v(12, 14.25) * mm, "end": v(88, 14.25) * mm});
            skLineSegment(sketch, "E5.0.37.2", {"start": v(12, 14.25) * mm, "end": v(12, 13.75) * mm});
            skLineSegment(sketch, "E5.0.37.3", {"start": v(88, 14.25) * mm, "end": v(88, 13.75) * mm});
            skLineSegment(sketch, "E5.1.1.0", {"start": v(12, 85.75) * mm, "end": v(88, 85.75) * mm});
            skLineSegment(sketch, "E5.1.1.1", {"start": v(12, 86.25) * mm, "end": v(88, 86.25) * mm});
            skLineSegment(sketch, "E5.1.1.2", {"start": v(12, 86.25) * mm, "end": v(12, 85.75) * mm});
            skLineSegment(sketch, "E5.1.1.3", {"start": v(88, 86.25) * mm, "end": v(88, 85.75) * mm});
            skLineSegment(sketch, "E5.1.2.0", {"start": v(12, 83.75) * mm, "end": v(88, 83.75) * mm});
            skLineSegment(sketch, "E5.1.2.1", {"start": v(12, 84.25) * mm, "end": v(88, 84.25) * mm});
            skLineSegment(sketch, "E5.1.2.2", {"start": v(12, 84.25) * mm, "end": v(12, 83.75) * mm});
            skLineSegment(sketch, "E5.1.2.3", {"start": v(88, 84.25) * mm, "end": v(88, 83.75) * mm});
            skLineSegment(sketch, "E5.1.3.0", {"start": v(12, 81.75) * mm, "end": v(88, 81.75) * mm});
            skLineSegment(sketch, "E5.1.3.1", {"start": v(12, 82.25) * mm, "end": v(88, 82.25) * mm});
            skLineSegment(sketch, "E5.1.3.2", {"start": v(12, 82.25) * mm, "end": v(12, 81.75) * mm});
            skLineSegment(sketch, "E5.1.3.3", {"start": v(88, 82.25) * mm, "end": v(88, 81.75) * mm});
            skLineSegment(sketch, "E5.1.4.0", {"start": v(12, 79.75) * mm, "end": v(88, 79.75) * mm});
            skLineSegment(sketch, "E5.1.4.1", {"start": v(12, 80.25) * mm, "end": v(88, 80.25) * mm});
            skLineSegment(sketch, "E5.1.4.2", {"start": v(12, 80.25) * mm, "end": v(12, 79.75) * mm});
            skLineSegment(sketch, "E5.1.4.3", {"start": v(88, 80.25) * mm, "end": v(88, 79.75) * mm});
            skLineSegment(sketch, "E5.1.5.0", {"start": v(12, 77.75) * mm, "end": v(88, 77.75) * mm});
            skLineSegment(sketch, "E5.1.5.1", {"start": v(12, 78.25) * mm, "end": v(88, 78.25) * mm});
            skLineSegment(sketch, "E5.1.5.2", {"start": v(12, 78.25) * mm, "end": v(12, 77.75) * mm});
            skLineSegment(sketch, "E5.1.5.3", {"start": v(88, 78.25) * mm, "end": v(88, 77.75) * mm});
            skLineSegment(sketch, "E5.1.6.0", {"start": v(12, 75.75) * mm, "end": v(88, 75.75) * mm});
            skLineSegment(sketch, "E5.1.6.1", {"start": v(12, 76.25) * mm, "end": v(88, 76.25) * mm});
            skLineSegment(sketch, "E5.1.6.2", {"start": v(12, 76.25) * mm, "end": v(12, 75.75) * mm});
            skLineSegment(sketch, "E5.1.6.3", {"start": v(88, 76.25) * mm, "end": v(88, 75.75) * mm});
            skLineSegment(sketch, "E5.1.7.0", {"start": v(12, 73.75) * mm, "end": v(88, 73.75) * mm});
            skLineSegment(sketch, "E5.1.7.1", {"start": v(12, 74.25) * mm, "end": v(88, 74.25) * mm});
            skLineSegment(sketch, "E5.1.7.2", {"start": v(12, 74.25) * mm, "end": v(12, 73.75) * mm});
            skLineSegment(sketch, "E5.1.7.3", {"start": v(88, 74.25) * mm, "end": v(88, 73.75) * mm});
            skLineSegment(sketch, "E5.1.8.0", {"start": v(12, 71.75) * mm, "end": v(88, 71.75) * mm});
            skLineSegment(sketch, "E5.1.8.1", {"start": v(12, 72.25) * mm, "end": v(88, 72.25) * mm});
            skLineSegment(sketch, "E5.1.8.2", {"start": v(12, 72.25) * mm, "end": v(12, 71.75) * mm});
            skLineSegment(sketch, "E5.1.8.3", {"start": v(88, 72.25) * mm, "end": v(88, 71.75) * mm});
            skLineSegment(sketch, "E5.1.9.0", {"start": v(12, 69.75) * mm, "end": v(88, 69.75) * mm});
            skLineSegment(sketch, "E5.1.9.1", {"start": v(12, 70.25) * mm, "end": v(88, 70.25) * mm});
            skLineSegment(sketch, "E5.1.9.2", {"start": v(12, 70.25) * mm, "end": v(12, 69.75) * mm});
            skLineSegment(sketch, "E5.1.9.3", {"start": v(88, 70.25) * mm, "end": v(88, 69.75) * mm});
            skLineSegment(sketch, "E5.1.10.0", {"start": v(12, 67.75) * mm, "end": v(88, 67.75) * mm});
            skLineSegment(sketch, "E5.1.10.1", {"start": v(12, 68.25) * mm, "end": v(88, 68.25) * mm});
            skLineSegment(sketch, "E5.1.10.2", {"start": v(12, 68.25) * mm, "end": v(12, 67.75) * mm});
            skLineSegment(sketch, "E5.1.10.3", {"start": v(88, 68.25) * mm, "end": v(88, 67.75) * mm});
            skLineSegment(sketch, "E5.1.11.0", {"start": v(12, 65.75) * mm, "end": v(88, 65.75) * mm});
            skLineSegment(sketch, "E5.1.11.1", {"start": v(12, 66.25) * mm, "end": v(88, 66.25) * mm});
            skLineSegment(sketch, "E5.1.11.2", {"start": v(12, 66.25) * mm, "end": v(12, 65.75) * mm});
            skLineSegment(sketch, "E5.1.11.3", {"start": v(88, 66.25) * mm, "end": v(88, 65.75) * mm});
            skLineSegment(sketch, "E5.1.12.0", {"start": v(12, 63.75) * mm, "end": v(88, 63.75) * mm});
            skLineSegment(sketch, "E5.1.12.1", {"start": v(12, 64.25) * mm, "end": v(88, 64.25) * mm});
            skLineSegment(sketch, "E5.1.12.2", {"start": v(12, 64.25) * mm, "end": v(12, 63.75) * mm});
            skLineSegment(sketch, "E5.1.12.3", {"start": v(88, 64.25) * mm, "end": v(88, 63.75) * mm});
            skLineSegment(sketch, "E5.1.13.0", {"start": v(12, 61.75) * mm, "end": v(88, 61.75) * mm});
            skLineSegment(sketch, "E5.1.13.1", {"start": v(12, 62.25) * mm, "end": v(88, 62.25) * mm});
            skLineSegment(sketch, "E5.1.13.2", {"start": v(12, 62.25) * mm, "end": v(12, 61.75) * mm});
            skLineSegment(sketch, "E5.1.13.3", {"start": v(88, 62.25) * mm, "end": v(88, 61.75) * mm});
            skLineSegment(sketch, "E5.1.14.0", {"start": v(12, 59.75) * mm, "end": v(88, 59.75) * mm});
            skLineSegment(sketch, "E5.1.14.1", {"start": v(12, 60.25) * mm, "end": v(88, 60.25) * mm});
            skLineSegment(sketch, "E5.1.14.2", {"start": v(12, 60.25) * mm, "end": v(12, 59.75) * mm});
            skLineSegment(sketch, "E5.1.14.3", {"start": v(88, 60.25) * mm, "end": v(88, 59.75) * mm});
            skLineSegment(sketch, "E5.1.15.0", {"start": v(12, 57.75) * mm, "end": v(88, 57.75) * mm});
            skLineSegment(sketch, "E5.1.15.1", {"start": v(12, 58.25) * mm, "end": v(88, 58.25) * mm});
            skLineSegment(sketch, "E5.1.15.2", {"start": v(12, 58.25) * mm, "end": v(12, 57.75) * mm});
            skLineSegment(sketch, "E5.1.15.3", {"start": v(88, 58.25) * mm, "end": v(88, 57.75) * mm});
            skLineSegment(sketch, "E5.1.16.0", {"start": v(12, 55.75) * mm, "end": v(88, 55.75) * mm});
            skLineSegment(sketch, "E5.1.16.1", {"start": v(12, 56.25) * mm, "end": v(88, 56.25) * mm});
            skLineSegment(sketch, "E5.1.16.2", {"start": v(12, 56.25) * mm, "end": v(12, 55.75) * mm});
            skLineSegment(sketch, "E5.1.16.3", {"start": v(88, 56.25) * mm, "end": v(88, 55.75) * mm});
            skLineSegment(sketch, "E5.1.17.0", {"start": v(12, 53.75) * mm, "end": v(88, 53.75) * mm});
            skLineSegment(sketch, "E5.1.17.1", {"start": v(12, 54.25) * mm, "end": v(88, 54.25) * mm});
            skLineSegment(sketch, "E5.1.17.2", {"start": v(12, 54.25) * mm, "end": v(12, 53.75) * mm});
            skLineSegment(sketch, "E5.1.17.3", {"start": v(88, 54.25) * mm, "end": v(88, 53.75) * mm});
            skLineSegment(sketch, "E5.1.18.0", {"start": v(12, 51.75) * mm, "end": v(88, 51.75) * mm});
            skLineSegment(sketch, "E5.1.18.1", {"start": v(12, 52.25) * mm, "end": v(88, 52.25) * mm});
            skLineSegment(sketch, "E5.1.18.2", {"start": v(12, 52.25) * mm, "end": v(12, 51.75) * mm});
            skLineSegment(sketch, "E5.1.18.3", {"start": v(88, 52.25) * mm, "end": v(88, 51.75) * mm});
            skLineSegment(sketch, "E5.1.19.0", {"start": v(12, 49.75) * mm, "end": v(88, 49.75) * mm});
            skLineSegment(sketch, "E5.1.19.1", {"start": v(12, 50.25) * mm, "end": v(88, 50.25) * mm});
            skLineSegment(sketch, "E5.1.19.2", {"start": v(12, 50.25) * mm, "end": v(12, 49.75) * mm});
            skLineSegment(sketch, "E5.1.19.3", {"start": v(88, 50.25) * mm, "end": v(88, 49.75) * mm});
            skLineSegment(sketch, "E5.1.20.0", {"start": v(12, 47.75) * mm, "end": v(88, 47.75) * mm});
            skLineSegment(sketch, "E5.1.20.1", {"start": v(12, 48.25) * mm, "end": v(88, 48.25) * mm});
            skLineSegment(sketch, "E5.1.20.2", {"start": v(12, 48.25) * mm, "end": v(12, 47.75) * mm});
            skLineSegment(sketch, "E5.1.20.3", {"start": v(88, 48.25) * mm, "end": v(88, 47.75) * mm});
            skLineSegment(sketch, "E5.1.21.0", {"start": v(12, 45.75) * mm, "end": v(88, 45.75) * mm});
            skLineSegment(sketch, "E5.1.21.1", {"start": v(12, 46.25) * mm, "end": v(88, 46.25) * mm});
            skLineSegment(sketch, "E5.1.21.2", {"start": v(12, 46.25) * mm, "end": v(12, 45.75) * mm});
            skLineSegment(sketch, "E5.1.21.3", {"start": v(88, 46.25) * mm, "end": v(88, 45.75) * mm});
            skLineSegment(sketch, "E5.1.22.0", {"start": v(12, 43.75) * mm, "end": v(88, 43.75) * mm});
            skLineSegment(sketch, "E5.1.22.1", {"start": v(12, 44.25) * mm, "end": v(88, 44.25) * mm});
            skLineSegment(sketch, "E5.1.22.2", {"start": v(12, 44.25) * mm, "end": v(12, 43.75) * mm});
            skLineSegment(sketch, "E5.1.22.3", {"start": v(88, 44.25) * mm, "end": v(88, 43.75) * mm});
            skLineSegment(sketch, "E5.1.23.0", {"start": v(12, 41.75) * mm, "end": v(88, 41.75) * mm});
            skLineSegment(sketch, "E5.1.23.1", {"start": v(12, 42.25) * mm, "end": v(88, 42.25) * mm});
            skLineSegment(sketch, "E5.1.23.2", {"start": v(12, 42.25) * mm, "end": v(12, 41.75) * mm});
            skLineSegment(sketch, "E5.1.23.3", {"start": v(88, 42.25) * mm, "end": v(88, 41.75) * mm});
            skLineSegment(sketch, "E5.1.24.0", {"start": v(12, 39.75) * mm, "end": v(88, 39.75) * mm});
            skLineSegment(sketch, "E5.1.24.1", {"start": v(12, 40.25) * mm, "end": v(88, 40.25) * mm});
            skLineSegment(sketch, "E5.1.24.2", {"start": v(12, 40.25) * mm, "end": v(12, 39.75) * mm});
            skLineSegment(sketch, "E5.1.24.3", {"start": v(88, 40.25) * mm, "end": v(88, 39.75) * mm});
            skLineSegment(sketch, "E5.1.25.0", {"start": v(12, 37.75) * mm, "end": v(88, 37.75) * mm});
            skLineSegment(sketch, "E5.1.25.1", {"start": v(12, 38.25) * mm, "end": v(88, 38.25) * mm});
            skLineSegment(sketch, "E5.1.25.2", {"start": v(12, 38.25) * mm, "end": v(12, 37.75) * mm});
            skLineSegment(sketch, "E5.1.25.3", {"start": v(88, 38.25) * mm, "end": v(88, 37.75) * mm});
            skLineSegment(sketch, "E5.1.26.0", {"start": v(12, 35.75) * mm, "end": v(88, 35.75) * mm});
            skLineSegment(sketch, "E5.1.26.1", {"start": v(12, 36.25) * mm, "end": v(88, 36.25) * mm});
            skLineSegment(sketch, "E5.1.26.2", {"start": v(12, 36.25) * mm, "end": v(12, 35.75) * mm});
            skLineSegment(sketch, "E5.1.26.3", {"start": v(88, 36.25) * mm, "end": v(88, 35.75) * mm});
            skLineSegment(sketch, "E5.1.27.0", {"start": v(12, 33.75) * mm, "end": v(88, 33.75) * mm});
            skLineSegment(sketch, "E5.1.27.1", {"start": v(12, 34.25) * mm, "end": v(88, 34.25) * mm});
            skLineSegment(sketch, "E5.1.27.2", {"start": v(12, 34.25) * mm, "end": v(12, 33.75) * mm});
            skLineSegment(sketch, "E5.1.27.3", {"start": v(88, 34.25) * mm, "end": v(88, 33.75) * mm});
            skLineSegment(sketch, "E5.1.28.0", {"start": v(12, 31.75) * mm, "end": v(88, 31.75) * mm});
            skLineSegment(sketch, "E5.1.28.1", {"start": v(12, 32.25) * mm, "end": v(88, 32.25) * mm});
            skLineSegment(sketch, "E5.1.28.2", {"start": v(12, 32.25) * mm, "end": v(12, 31.75) * mm});
            skLineSegment(sketch, "E5.1.28.3", {"start": v(88, 32.25) * mm, "end": v(88, 31.75) * mm});
            skLineSegment(sketch, "E5.1.29.0", {"start": v(12, 29.75) * mm, "end": v(88, 29.75) * mm});
            skLineSegment(sketch, "E5.1.29.1", {"start": v(12, 30.25) * mm, "end": v(88, 30.25) * mm});
            skLineSegment(sketch, "E5.1.29.2", {"start": v(12, 30.25) * mm, "end": v(12, 29.75) * mm});
            skLineSegment(sketch, "E5.1.29.3", {"start": v(88, 30.25) * mm, "end": v(88, 29.75) * mm});
            skLineSegment(sketch, "E5.1.30.0", {"start": v(12, 27.75) * mm, "end": v(88, 27.75) * mm});
            skLineSegment(sketch, "E5.1.30.1", {"start": v(12, 28.25) * mm, "end": v(88, 28.25) * mm});
            skLineSegment(sketch, "E5.1.30.2", {"start": v(12, 28.25) * mm, "end": v(12, 27.75) * mm});
            skLineSegment(sketch, "E5.1.30.3", {"start": v(88, 28.25) * mm, "end": v(88, 27.75) * mm});
            skLineSegment(sketch, "E5.1.31.0", {"start": v(12, 25.75) * mm, "end": v(88, 25.75) * mm});
            skLineSegment(sketch, "E5.1.31.1", {"start": v(12, 26.25) * mm, "end": v(88, 26.25) * mm});
            skLineSegment(sketch, "E5.1.31.2", {"start": v(12, 26.25) * mm, "end": v(12, 25.75) * mm});
            skLineSegment(sketch, "E5.1.31.3", {"start": v(88, 26.25) * mm, "end": v(88, 25.75) * mm});
            skLineSegment(sketch, "E5.1.32.0", {"start": v(12, 23.75) * mm, "end": v(88, 23.75) * mm});
            skLineSegment(sketch, "E5.1.32.1", {"start": v(12, 24.25) * mm, "end": v(88, 24.25) * mm});
            skLineSegment(sketch, "E5.1.32.2", {"start": v(12, 24.25) * mm, "end": v(12, 23.75) * mm});
            skLineSegment(sketch, "E5.1.32.3", {"start": v(88, 24.25) * mm, "end": v(88, 23.75) * mm});
            skLineSegment(sketch, "E5.1.33.0", {"start": v(12, 21.75) * mm, "end": v(88, 21.75) * mm});
            skLineSegment(sketch, "E5.1.33.1", {"start": v(12, 22.25) * mm, "end": v(88, 22.25) * mm});
            skLineSegment(sketch, "E5.1.33.2", {"start": v(12, 22.25) * mm, "end": v(12, 21.75) * mm});
            skLineSegment(sketch, "E5.1.33.3", {"start": v(88, 22.25) * mm, "end": v(88, 21.75) * mm});
            skLineSegment(sketch, "E5.1.34.0", {"start": v(12, 19.75) * mm, "end": v(88, 19.75) * mm});
            skLineSegment(sketch, "E5.1.34.1", {"start": v(12, 20.25) * mm, "end": v(88, 20.25) * mm});
            skLineSegment(sketch, "E5.1.34.2", {"start": v(12, 20.25) * mm, "end": v(12, 19.75) * mm});
            skLineSegment(sketch, "E5.1.34.3", {"start": v(88, 20.25) * mm, "end": v(88, 19.75) * mm});
            skLineSegment(sketch, "E5.1.35.0", {"start": v(12, 17.75) * mm, "end": v(88, 17.75) * mm});
            skLineSegment(sketch, "E5.1.35.1", {"start": v(12, 18.25) * mm, "end": v(88, 18.25) * mm});
            skLineSegment(sketch, "E5.1.35.2", {"start": v(12, 18.25) * mm, "end": v(12, 17.75) * mm});
            skLineSegment(sketch, "E5.1.35.3", {"start": v(88, 18.25) * mm, "end": v(88, 17.75) * mm});
            skLineSegment(sketch, "E5.1.36.0", {"start": v(12, 15.75) * mm, "end": v(88, 15.75) * mm});
            skLineSegment(sketch, "E5.1.36.1", {"start": v(12, 16.25) * mm, "end": v(88, 16.25) * mm});
            skLineSegment(sketch, "E5.1.36.2", {"start": v(12, 16.25) * mm, "end": v(12, 15.75) * mm});
            skLineSegment(sketch, "E5.1.36.3", {"start": v(88, 16.25) * mm, "end": v(88, 15.75) * mm});
            skLineSegment(sketch, "E5.1.37.0", {"start": v(12, 13.75) * mm, "end": v(88, 13.75) * mm});
            skLineSegment(sketch, "E5.1.37.1", {"start": v(12, 14.25) * mm, "end": v(88, 14.25) * mm});
            skLineSegment(sketch, "E5.1.37.2", {"start": v(12, 14.25) * mm, "end": v(12, 13.75) * mm});
            skLineSegment(sketch, "E5.1.37.3", {"start": v(88, 14.25) * mm, "end": v(88, 13.75) * mm});
            skLineSegment(sketch, "E5.direction1", {"start": v(12, 87.75) * mm, "end": v(12, 87.75) * mm});
            skLineSegment(sketch, "E5.direction2", {"start": v(12, 87.75) * mm, "end": v(12, 85.75) * mm, "construction": true});
            skLineSegment(sketch, "E6.0.0.38", {"start": v(12, 11.75) * mm, "end": v(88, 11.75) * mm});
            skLineSegment(sketch, "E6.3.0.38", {"start": v(12, 12.25) * mm, "end": v(88, 12.25) * mm});
            skLineSegment(sketch, "E6.6.0.38", {"start": v(12, 12.25) * mm, "end": v(12, 11.75) * mm});
            skLineSegment(sketch, "E6.9.0.38", {"start": v(88, 12.25) * mm, "end": v(88, 11.75) * mm});
            skLineSegment(sketch, "E6.0.1.38", {"start": v(12, 11.75) * mm, "end": v(88, 11.75) * mm});
            skLineSegment(sketch, "E6.3.1.38", {"start": v(12, 12.25) * mm, "end": v(88, 12.25) * mm});
            skLineSegment(sketch, "E6.6.1.38", {"start": v(12, 12.25) * mm, "end": v(12, 11.75) * mm});
            skLineSegment(sketch, "E6.9.1.38", {"start": v(88, 12.25) * mm, "end": v(88, 11.75) * mm});
            skSolve(sketch);
        }
        {
            var Q0;
            Q0 = qSketchRegion(id + "F6", true);
            extrude(context, id + "F7", {"entities" : qUnion([Q0]), "operationType" : NewBodyOperationType.REMOVE, "oppositeDirection" : true, "depth" : 0.2 * mm});
        }
    });
